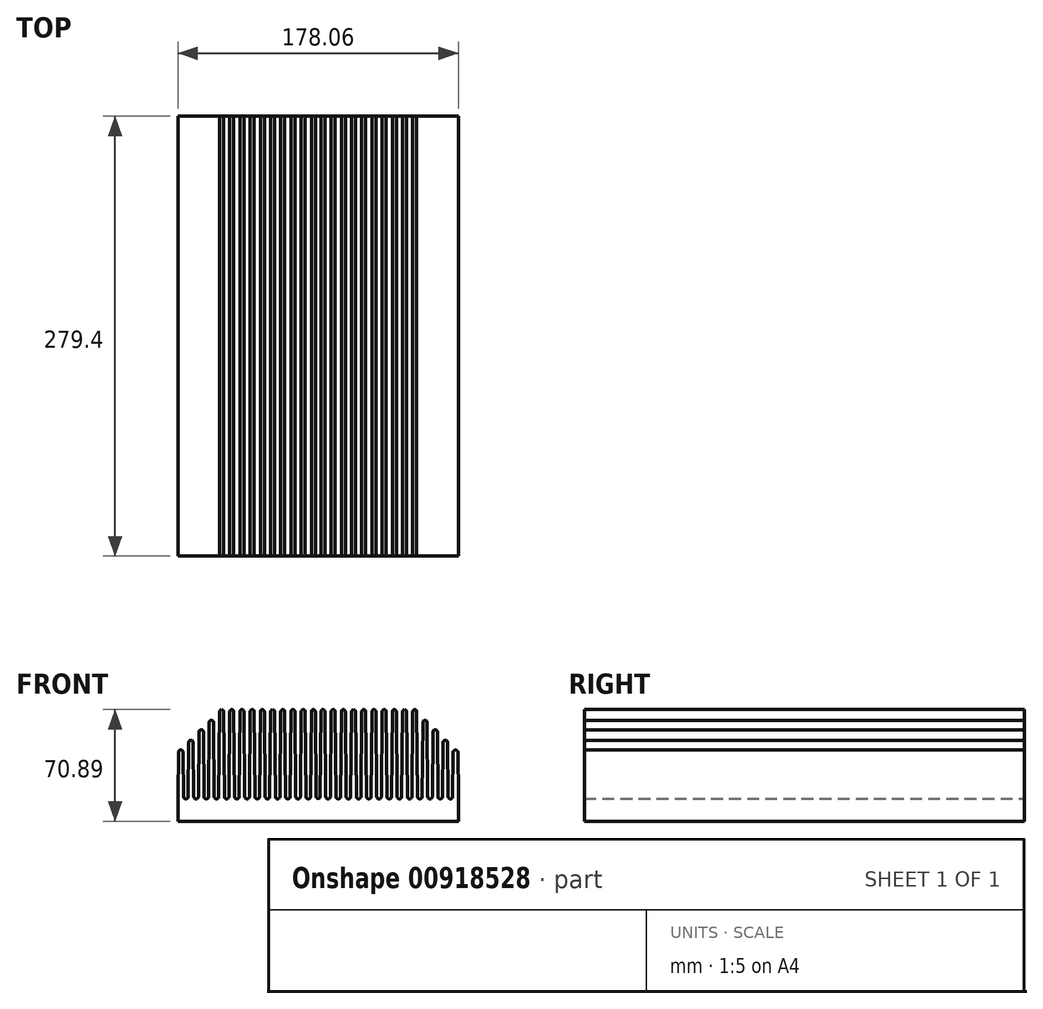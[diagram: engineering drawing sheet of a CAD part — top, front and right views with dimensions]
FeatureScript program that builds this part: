
annotation { "Feature Type Name" : "Feature", "Feature Type Description" : "" }
export const myFeature = defineFeature(function(context is Context, id is Id, definition is map)
    precondition{}
    {
        {
            var Q0;
            Q0=qCreatedBy(makeId("Front.planeOp"),FACE);
            var sketch = newSketch(context, id + "F0", { "sketchPlane" : qUnion([Q0])});
            skSolve(sketch);
        }
        {
            var Q0;
            Q0=qCreatedBy(makeId("Front.planeOp"),FACE);
            var sketch = newSketch(context, id + "F1", { "sketchPlane" : qUnion([Q0])});
            skLineSegment(sketch, "E0.top", {"start": v(88.9, 13.33) * mm, "end": v(177.93, 13.33) * mm});
            skLineSegment(sketch, "E1", {"start": v(88.9, 13.33) * mm, "end": v(88.9, 0) * mm});
            skLineSegment(sketch, "E2", {"start": v(90.17, 15.64) * mm, "end": v(90.68, 69.62) * mm});
            skArc(sketch, "E3", {"start": v(93.22, 69.62) * mm, "mid": v(91.95, 70.89) * mm, "end": v(90.68, 69.62) * mm});
            skLineSegment(sketch, "E4", {"start": v(93.22, 69.62) * mm, "end": v(93.73, 15.64) * mm});
            skLineSegment(sketch, "E5", {"start": v(91.95, 15.64) * mm, "end": v(91.95, 69.62) * mm});
            skLineSegment(sketch, "E6", {"start": v(90.17, 15.64) * mm, "end": v(91.95, 15.64) * mm});
            skLineSegment(sketch, "E7", {"start": v(93.73, 15.64) * mm, "end": v(91.95, 15.64) * mm});
            skArc(sketch, "E8.1.0.0", {"start": v(99.7, 69.62) * mm, "mid": v(98.43, 70.89) * mm, "end": v(97.16, 69.62) * mm});
            skLineSegment(sketch, "E8.1.0.1", {"start": v(98.42, 15.64) * mm, "end": v(98.42, 69.62) * mm});
            skLineSegment(sketch, "E8.1.0.2", {"start": v(96.65, 15.64) * mm, "end": v(97.15, 69.62) * mm});
            skLineSegment(sketch, "E8.1.0.3", {"start": v(99.7, 69.62) * mm, "end": v(100.2, 15.64) * mm});
            skArc(sketch, "E8.2.0.0", {"start": v(106.17, 69.62) * mm, "mid": v(104.9, 70.89) * mm, "end": v(103.63, 69.62) * mm});
            skLineSegment(sketch, "E8.2.0.1", {"start": v(104.9, 15.64) * mm, "end": v(104.9, 69.62) * mm});
            skLineSegment(sketch, "E8.2.0.2", {"start": v(103.12, 15.64) * mm, "end": v(103.63, 69.62) * mm});
            skLineSegment(sketch, "E8.2.0.3", {"start": v(106.17, 69.62) * mm, "end": v(106.68, 15.64) * mm});
            skArc(sketch, "E8.3.0.0", {"start": v(112.65, 69.62) * mm, "mid": v(111.38, 70.89) * mm, "end": v(110.1, 69.62) * mm});
            skLineSegment(sketch, "E8.3.0.1", {"start": v(111.38, 15.64) * mm, "end": v(111.38, 69.62) * mm});
            skLineSegment(sketch, "E8.3.0.2", {"start": v(109.6, 15.64) * mm, "end": v(110.1, 69.62) * mm});
            skLineSegment(sketch, "E8.3.0.3", {"start": v(112.65, 69.62) * mm, "end": v(113.16, 15.64) * mm});
            skArc(sketch, "E8.4.0.0", {"start": v(119.13, 69.62) * mm, "mid": v(117.86, 70.89) * mm, "end": v(116.59, 69.62) * mm});
            skLineSegment(sketch, "E8.4.0.1", {"start": v(117.86, 15.64) * mm, "end": v(117.86, 69.62) * mm});
            skLineSegment(sketch, "E8.4.0.2", {"start": v(116.08, 15.64) * mm, "end": v(116.59, 69.62) * mm});
            skLineSegment(sketch, "E8.4.0.3", {"start": v(119.13, 69.62) * mm, "end": v(119.63, 15.64) * mm});
            skArc(sketch, "E8.5.0.0", {"start": v(125.6, 69.62) * mm, "mid": v(124.33, 70.89) * mm, "end": v(123.06, 69.62) * mm});
            skLineSegment(sketch, "E8.5.0.1", {"start": v(124.33, 15.64) * mm, "end": v(124.33, 69.62) * mm});
            skLineSegment(sketch, "E8.5.0.2", {"start": v(122.55, 15.64) * mm, "end": v(123.06, 69.62) * mm});
            skLineSegment(sketch, "E8.5.0.3", {"start": v(125.6, 69.62) * mm, "end": v(126.11, 15.64) * mm});
            skArc(sketch, "E8.6.0.0", {"start": v(132.08, 69.62) * mm, "mid": v(130.8, 70.89) * mm, "end": v(129.54, 69.62) * mm});
            skLineSegment(sketch, "E8.6.0.1", {"start": v(130.8, 15.64) * mm, "end": v(130.8, 69.62) * mm});
            skLineSegment(sketch, "E8.6.0.2", {"start": v(129.03, 15.64) * mm, "end": v(129.54, 69.62) * mm});
            skLineSegment(sketch, "E8.6.0.3", {"start": v(132.08, 69.62) * mm, "end": v(132.59, 15.64) * mm});
            skArc(sketch, "E8.7.0.0", {"start": v(138.56, 69.62) * mm, "mid": v(137.29, 70.89) * mm, "end": v(136.02, 69.62) * mm});
            skLineSegment(sketch, "E8.7.0.1", {"start": v(137.29, 15.64) * mm, "end": v(137.29, 69.62) * mm});
            skLineSegment(sketch, "E8.7.0.2", {"start": v(135.5, 15.64) * mm, "end": v(136.02, 69.62) * mm});
            skLineSegment(sketch, "E8.7.0.3", {"start": v(138.56, 69.62) * mm, "end": v(139.06, 15.64) * mm});
            skArc(sketch, "E8.8.0.0", {"start": v(145.03, 69.62) * mm, "mid": v(143.76, 70.89) * mm, "end": v(142.5, 69.62) * mm});
            skLineSegment(sketch, "E8.8.0.1", {"start": v(143.76, 15.64) * mm, "end": v(143.76, 69.62) * mm});
            skLineSegment(sketch, "E8.8.0.2", {"start": v(141.99, 15.64) * mm, "end": v(142.5, 69.62) * mm});
            skLineSegment(sketch, "E8.8.0.3", {"start": v(145.03, 69.62) * mm, "end": v(145.54, 15.64) * mm});
            skArc(sketch, "E8.9.0.0", {"start": v(151.51, 69.62) * mm, "mid": v(150.24, 70.89) * mm, "end": v(148.97, 69.62) * mm});
            skLineSegment(sketch, "E8.9.0.1", {"start": v(150.24, 15.64) * mm, "end": v(150.24, 69.62) * mm});
            skLineSegment(sketch, "E8.9.0.2", {"start": v(148.46, 15.64) * mm, "end": v(148.97, 69.62) * mm});
            skLineSegment(sketch, "E8.9.0.3", {"start": v(151.51, 69.62) * mm, "end": v(152.02, 15.64) * mm});
            skLineSegment(sketch, "E8.10.0.1", {"start": v(156.72, 15.64) * mm, "end": v(156.72, 64.12) * mm});
            skLineSegment(sketch, "E8.10.0.2", {"start": v(154.94, 15.64) * mm, "end": v(155.38, 62.8) * mm});
            skLineSegment(sketch, "E8.10.0.3", {"start": v(158.05, 62.8) * mm, "end": v(158.5, 15.64) * mm});
            skLineSegment(sketch, "E8.11.0.1", {"start": v(163.2, 15.64) * mm, "end": v(163.2, 58.12) * mm});
            skLineSegment(sketch, "E8.11.0.2", {"start": v(161.42, 15.64) * mm, "end": v(161.8, 56.74) * mm});
            skLineSegment(sketch, "E8.11.0.3", {"start": v(164.59, 56.74) * mm, "end": v(164.97, 15.64) * mm});
            skLineSegment(sketch, "E8.12.0.1", {"start": v(169.67, 15.64) * mm, "end": v(169.67, 51.5) * mm});
            skLineSegment(sketch, "E8.12.0.2", {"start": v(167.9, 15.64) * mm, "end": v(168.22, 50.05) * mm});
            skLineSegment(sketch, "E8.12.0.3", {"start": v(171.13, 50.05) * mm, "end": v(171.45, 15.64) * mm});
            skLineSegment(sketch, "E8.13.0.1", {"start": v(176.15, 15.64) * mm, "end": v(176.15, 45.24) * mm});
            skLineSegment(sketch, "E8.13.0.2", {"start": v(174.37, 15.64) * mm, "end": v(174.64, 43.74) * mm});
            skLineSegment(sketch, "E8.13.0.3", {"start": v(177.66, 43.74) * mm, "end": v(177.93, 15.64) * mm});
            skLineSegment(sketch, "E8.direction1", {"start": v(90.17, 15.64) * mm, "end": v(96.65, 15.64) * mm, "construction": true});
            skArc(sketch, "E9", {"start": v(158.05, 62.8) * mm, "mid": v(156.72, 64.12) * mm, "end": v(155.38, 62.8) * mm});
            skArc(sketch, "E10", {"start": v(164.59, 56.74) * mm, "mid": v(163.2, 58.12) * mm, "end": v(161.8, 56.74) * mm});
            skArc(sketch, "E11", {"start": v(171.13, 50.05) * mm, "mid": v(169.67, 51.5) * mm, "end": v(168.22, 50.05) * mm});
            skArc(sketch, "E12", {"start": v(177.66, 43.74) * mm, "mid": v(176.15, 45.24) * mm, "end": v(174.64, 43.74) * mm});
            skLineSegment(sketch, "E13", {"start": v(177.93, 13.78) * mm, "end": v(177.93, 15.64) * mm});
            skLineSegment(sketch, "E14", {"start": v(177.93, 13.78) * mm, "end": v(177.93, 0) * mm});
            skLineSegment(sketch, "E15", {"start": v(177.93, 0) * mm, "end": v(177.8, 0) * mm});
            skArc(sketch, "E16", {"start": v(100.2, 15.64) * mm, "mid": v(101.66, 14.2) * mm, "end": v(103.12, 15.64) * mm});
            skPoint(sketch, "E16.third.point", {"position": v(101.71, 14.2) * mm});
            skArc(sketch, "E17.1.0.0", {"start": v(106.68, 15.64) * mm, "mid": v(108.14, 14.2) * mm, "end": v(109.6, 15.64) * mm});
            skArc(sketch, "E17.2.0.0", {"start": v(113.16, 15.64) * mm, "mid": v(114.62, 14.2) * mm, "end": v(116.08, 15.64) * mm});
            skArc(sketch, "E17.3.0.0", {"start": v(119.63, 15.64) * mm, "mid": v(121.1, 14.2) * mm, "end": v(122.55, 15.64) * mm});
            skArc(sketch, "E17.4.0.0", {"start": v(126.11, 15.64) * mm, "mid": v(127.57, 14.2) * mm, "end": v(129.03, 15.64) * mm});
            skArc(sketch, "E17.5.0.0", {"start": v(132.59, 15.64) * mm, "mid": v(134.05, 14.2) * mm, "end": v(135.5, 15.64) * mm});
            skArc(sketch, "E17.6.0.0", {"start": v(139.06, 15.64) * mm, "mid": v(140.53, 14.2) * mm, "end": v(141.99, 15.64) * mm});
            skArc(sketch, "E17.7.0.0", {"start": v(145.54, 15.64) * mm, "mid": v(147, 14.2) * mm, "end": v(148.46, 15.64) * mm});
            skArc(sketch, "E17.8.0.0", {"start": v(152.02, 15.64) * mm, "mid": v(153.48, 14.2) * mm, "end": v(154.94, 15.64) * mm});
            skArc(sketch, "E17.9.0.0", {"start": v(158.5, 15.64) * mm, "mid": v(159.96, 14.2) * mm, "end": v(161.42, 15.64) * mm});
            skArc(sketch, "E17.10.0.0", {"start": v(164.97, 15.64) * mm, "mid": v(166.43, 14.2) * mm, "end": v(167.9, 15.64) * mm});
            skArc(sketch, "E17.11.0.0", {"start": v(171.45, 15.64) * mm, "mid": v(172.91, 14.2) * mm, "end": v(174.37, 15.64) * mm});
            skLineSegment(sketch, "E17.direction1", {"start": v(100.2, 15.64) * mm, "end": v(106.68, 15.64) * mm, "construction": true});
            skArc(sketch, "E18.MirrorCS", {"start": v(96.65, 15.64) * mm, "mid": v(95.19, 14.2) * mm, "end": v(93.73, 15.64) * mm});
            skLineSegment(sketch, "E19", {"start": v(88.9, 0) * mm, "end": v(177.8, 0) * mm});
            skArc(sketch, "E20.MirrorCS", {"start": v(81.15, 15.64) * mm, "mid": v(82.61, 14.2) * mm, "end": v(84.07, 15.64) * mm});
            skLineSegment(sketch, "E21.MirrorCS", {"start": v(-0.13, 0) * mm, "end": v(0, 0) * mm});
            skLineSegment(sketch, "E22.MirrorCS", {"start": v(84.07, 15.64) * mm, "end": v(85.85, 15.64) * mm});
            skLineSegment(sketch, "E23.MirrorCS", {"start": v(87.63, 15.64) * mm, "end": v(81.15, 15.64) * mm, "construction": true});
            skArc(sketch, "E24.MirrorCS", {"start": v(71.63, 69.62) * mm, "mid": v(72.9, 70.89) * mm, "end": v(74.17, 69.62) * mm});
            skArc(sketch, "E25.MirrorCS", {"start": v(58.67, 69.62) * mm, "mid": v(59.94, 70.89) * mm, "end": v(61.21, 69.62) * mm});
            skArc(sketch, "E26.MirrorCS", {"start": v(32.77, 69.62) * mm, "mid": v(34.04, 70.89) * mm, "end": v(35.3, 69.62) * mm});
            skArc(sketch, "E27.MirrorCS", {"start": v(71.12, 15.64) * mm, "mid": v(69.66, 14.2) * mm, "end": v(68.2, 15.64) * mm});
            skArc(sketch, "E28.MirrorCS", {"start": v(78.1, 69.62) * mm, "mid": v(79.38, 70.89) * mm, "end": v(80.64, 69.62) * mm});
            skArc(sketch, "E29.MirrorCS", {"start": v(38.74, 15.64) * mm, "mid": v(37.27, 14.2) * mm, "end": v(35.81, 15.64) * mm});
            skArc(sketch, "E30.MirrorCS", {"start": v(32.26, 15.64) * mm, "mid": v(30.8, 14.2) * mm, "end": v(29.34, 15.64) * mm});
            skArc(sketch, "E31.MirrorCS", {"start": v(25.78, 15.64) * mm, "mid": v(24.32, 14.2) * mm, "end": v(22.86, 15.64) * mm});
            skArc(sketch, "E32.MirrorCS", {"start": v(77.6, 15.64) * mm, "mid": v(76.14, 14.2) * mm, "end": v(74.68, 15.64) * mm});
            skArc(sketch, "E33.MirrorCS", {"start": v(45.21, 15.64) * mm, "mid": v(43.75, 14.2) * mm, "end": v(42.3, 15.64) * mm});
            skLineSegment(sketch, "E34.MirrorCS", {"start": v(77.6, 15.64) * mm, "end": v(71.12, 15.64) * mm, "construction": true});
            skArc(sketch, "E35.MirrorCS", {"start": v(65.15, 69.62) * mm, "mid": v(66.42, 70.89) * mm, "end": v(67.7, 69.62) * mm});
            skArc(sketch, "E36.MirrorCS", {"start": v(45.72, 69.62) * mm, "mid": v(47, 70.89) * mm, "end": v(48.26, 69.62) * mm});
            skArc(sketch, "E37.MirrorCS", {"start": v(64.64, 15.64) * mm, "mid": v(63.18, 14.2) * mm, "end": v(61.72, 15.64) * mm});
            skArc(sketch, "E38.MirrorCS", {"start": v(52.2, 69.62) * mm, "mid": v(53.47, 70.89) * mm, "end": v(54.74, 69.62) * mm});
            skArc(sketch, "E39.MirrorCS", {"start": v(58.17, 15.64) * mm, "mid": v(56.7, 14.2) * mm, "end": v(55.25, 15.64) * mm});
            skLineSegment(sketch, "E40.MirrorCS", {"start": v(-0.13, 13.78) * mm, "end": v(-0.13, 15.64) * mm});
            skLineSegment(sketch, "E41.MirrorCS", {"start": v(87.63, 15.64) * mm, "end": v(85.85, 15.64) * mm});
            skArc(sketch, "E42.MirrorCS", {"start": v(84.58, 69.62) * mm, "mid": v(85.85, 70.89) * mm, "end": v(87.12, 69.62) * mm});
            skArc(sketch, "E43.MirrorCS", {"start": v(39.24, 69.62) * mm, "mid": v(40.51, 70.89) * mm, "end": v(41.78, 69.62) * mm});
            skArc(sketch, "E44.MirrorCS", {"start": v(12.83, 15.64) * mm, "mid": v(11.37, 14.2) * mm, "end": v(9.9, 15.64) * mm});
            skArc(sketch, "E45.MirrorCS", {"start": v(0.14, 43.74) * mm, "mid": v(1.65, 45.24) * mm, "end": v(3.16, 43.74) * mm});
            skArc(sketch, "E46.MirrorCS", {"start": v(19.75, 62.8) * mm, "mid": v(21.08, 64.12) * mm, "end": v(22.42, 62.8) * mm});
            skArc(sketch, "E47.MirrorCS", {"start": v(26.29, 69.62) * mm, "mid": v(27.56, 70.89) * mm, "end": v(28.83, 69.62) * mm});
            skArc(sketch, "E48.MirrorCS", {"start": v(6.67, 50.05) * mm, "mid": v(8.13, 51.5) * mm, "end": v(9.58, 50.05) * mm});
            skArc(sketch, "E49.MirrorCS", {"start": v(13.21, 56.74) * mm, "mid": v(14.6, 58.12) * mm, "end": v(16, 56.74) * mm});
            skArc(sketch, "E50.MirrorCS", {"start": v(6.35, 15.64) * mm, "mid": v(4.89, 14.2) * mm, "end": v(3.43, 15.64) * mm});
            skArc(sketch, "E51.MirrorCS", {"start": v(51.69, 15.64) * mm, "mid": v(50.23, 14.2) * mm, "end": v(48.77, 15.64) * mm});
            skLineSegment(sketch, "E52.MirrorCS", {"start": v(88.9, 13.33) * mm, "end": v(-0.13, 13.33) * mm});
            skArc(sketch, "E53.MirrorCS", {"start": v(19.3, 15.64) * mm, "mid": v(17.84, 14.2) * mm, "end": v(16.38, 15.64) * mm});
            skLineSegment(sketch, "E54.MirrorCS", {"start": v(85.85, 15.64) * mm, "end": v(85.85, 69.62) * mm});
            skLineSegment(sketch, "E55.MirrorCS", {"start": v(59.94, 15.64) * mm, "end": v(59.94, 69.62) * mm});
            skLineSegment(sketch, "E56.MirrorCS", {"start": v(0.14, 43.74) * mm, "end": v(-0.13, 15.64) * mm});
            skLineSegment(sketch, "E57.MirrorCS", {"start": v(87.63, 15.64) * mm, "end": v(87.12, 69.62) * mm});
            skLineSegment(sketch, "E58.MirrorCS", {"start": v(29.34, 15.64) * mm, "end": v(28.83, 69.62) * mm});
            skLineSegment(sketch, "E59.MirrorCS", {"start": v(8.13, 15.64) * mm, "end": v(8.13, 51.5) * mm});
            skLineSegment(sketch, "E60.MirrorCS", {"start": v(3.43, 15.64) * mm, "end": v(3.16, 43.74) * mm});
            skLineSegment(sketch, "E61.MirrorCS", {"start": v(48.77, 15.64) * mm, "end": v(48.26, 69.62) * mm});
            skLineSegment(sketch, "E62.MirrorCS", {"start": v(39.24, 69.62) * mm, "end": v(38.74, 15.64) * mm});
            skPoint(sketch, "E63.MirrorP", {"position": v(76.09, 14.2) * mm});
            skLineSegment(sketch, "E64.MirrorCS", {"start": v(6.67, 50.05) * mm, "end": v(6.35, 15.64) * mm});
            skLineSegment(sketch, "E65.MirrorCS", {"start": v(16.38, 15.64) * mm, "end": v(16, 56.74) * mm});
            skLineSegment(sketch, "E66.MirrorCS", {"start": v(58.67, 69.62) * mm, "end": v(58.17, 15.64) * mm});
            skLineSegment(sketch, "E67.MirrorCS", {"start": v(61.72, 15.64) * mm, "end": v(61.21, 69.62) * mm});
            skLineSegment(sketch, "E68.MirrorCS", {"start": v(9.9, 15.64) * mm, "end": v(9.58, 50.05) * mm});
            skLineSegment(sketch, "E69.MirrorCS", {"start": v(13.21, 56.74) * mm, "end": v(12.83, 15.64) * mm});
            skLineSegment(sketch, "E70.MirrorCS", {"start": v(40.51, 15.64) * mm, "end": v(40.51, 69.62) * mm});
            skLineSegment(sketch, "E71.MirrorCS", {"start": v(84.58, 69.62) * mm, "end": v(84.07, 15.64) * mm});
            skLineSegment(sketch, "E72.MirrorCS", {"start": v(35.81, 15.64) * mm, "end": v(35.3, 69.62) * mm});
            skLineSegment(sketch, "E73.MirrorCS", {"start": v(72.9, 15.64) * mm, "end": v(72.9, 69.62) * mm});
            skLineSegment(sketch, "E74.MirrorCS", {"start": v(88.9, 0) * mm, "end": v(0, 0) * mm});
            skLineSegment(sketch, "E75.MirrorCS", {"start": v(55.25, 15.64) * mm, "end": v(54.74, 69.62) * mm});
            skLineSegment(sketch, "E76.MirrorCS", {"start": v(66.42, 15.64) * mm, "end": v(66.42, 69.62) * mm});
            skLineSegment(sketch, "E77.MirrorCS", {"start": v(79.38, 15.64) * mm, "end": v(79.38, 69.62) * mm});
            skLineSegment(sketch, "E78.MirrorCS", {"start": v(34.04, 15.64) * mm, "end": v(34.04, 69.62) * mm});
            skLineSegment(sketch, "E79.MirrorCS", {"start": v(52.2, 69.62) * mm, "end": v(51.69, 15.64) * mm});
            skLineSegment(sketch, "E80.MirrorCS", {"start": v(45.72, 69.62) * mm, "end": v(45.21, 15.64) * mm});
            skLineSegment(sketch, "E81.MirrorCS", {"start": v(53.47, 15.64) * mm, "end": v(53.47, 69.62) * mm});
            skLineSegment(sketch, "E82.MirrorCS", {"start": v(68.2, 15.64) * mm, "end": v(67.7, 69.62) * mm});
            skLineSegment(sketch, "E83.MirrorCS", {"start": v(42.3, 15.64) * mm, "end": v(41.78, 69.62) * mm});
            skLineSegment(sketch, "E84.MirrorCS", {"start": v(71.63, 69.62) * mm, "end": v(71.12, 15.64) * mm});
            skLineSegment(sketch, "E85.MirrorCS", {"start": v(22.86, 15.64) * mm, "end": v(22.42, 62.8) * mm});
            skLineSegment(sketch, "E86.MirrorCS", {"start": v(32.77, 69.62) * mm, "end": v(32.26, 15.64) * mm});
            skLineSegment(sketch, "E87.MirrorCS", {"start": v(47, 15.64) * mm, "end": v(47, 69.62) * mm});
            skLineSegment(sketch, "E88.MirrorCS", {"start": v(65.15, 69.62) * mm, "end": v(64.64, 15.64) * mm});
            skLineSegment(sketch, "E89.MirrorCS", {"start": v(-0.13, 13.78) * mm, "end": v(-0.13, 0) * mm});
            skLineSegment(sketch, "E90.MirrorCS", {"start": v(26.29, 69.62) * mm, "end": v(25.78, 15.64) * mm});
            skLineSegment(sketch, "E91.MirrorCS", {"start": v(1.65, 15.64) * mm, "end": v(1.65, 45.24) * mm});
            skLineSegment(sketch, "E92.MirrorCS", {"start": v(78.1, 69.62) * mm, "end": v(77.6, 15.64) * mm});
            skLineSegment(sketch, "E93.MirrorCS", {"start": v(81.15, 15.64) * mm, "end": v(80.64, 69.62) * mm});
            skLineSegment(sketch, "E94.MirrorCS", {"start": v(19.75, 62.8) * mm, "end": v(19.3, 15.64) * mm});
            skLineSegment(sketch, "E95.MirrorCS", {"start": v(27.56, 15.64) * mm, "end": v(27.56, 69.62) * mm});
            skLineSegment(sketch, "E96.MirrorCS", {"start": v(21.08, 15.64) * mm, "end": v(21.08, 64.12) * mm});
            skLineSegment(sketch, "E97.MirrorCS", {"start": v(14.6, 15.64) * mm, "end": v(14.6, 58.12) * mm});
            skLineSegment(sketch, "E98.MirrorCS", {"start": v(74.68, 15.64) * mm, "end": v(74.17, 69.62) * mm});
            skArc(sketch, "E99", {"start": v(87.63, 15.64) * mm, "mid": v(88.9, 14.38) * mm, "end": v(90.17, 15.64) * mm});
            skPoint(sketch, "E99.third.point", {"position": v(89.94, 14.92) * mm});
            skSolve(sketch);
        }
        {
            var Q0;
            Q0 = qSketchRegion(id + "F1", true);
            extrude(context, id + "F2", {"entities" : qUnion([Q0]), "depth" : 279.4 * mm, "offsetDistance" : 25.4 * mm});
        }
    });
